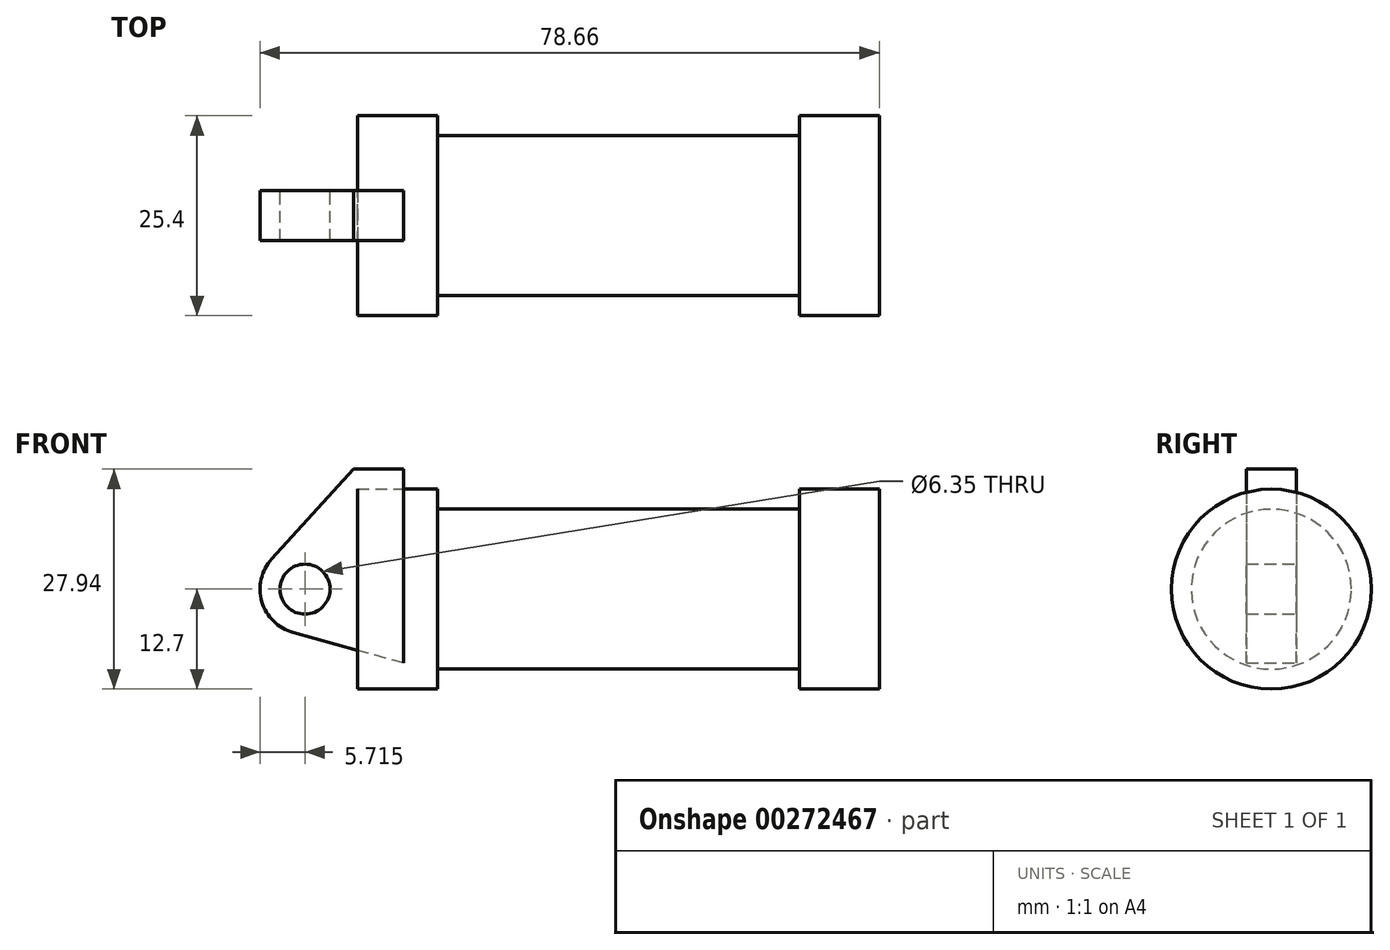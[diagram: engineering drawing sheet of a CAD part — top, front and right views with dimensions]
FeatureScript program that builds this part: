
annotation { "Feature Type Name" : "Feature", "Feature Type Description" : "" }
export const myFeature = defineFeature(function(context is Context, id is Id, definition is map)
    precondition{}
    {
        {
            var Q0;
            Q0=qCreatedBy(makeId("Front.planeOp"),FACE);
            var sketch = newSketch(context, id + "F0", { "sketchPlane" : qUnion([Q0])});
            skLineSegment(sketch, "E0", {"start": v(0, 0) * mm, "end": v(0, 12.7) * mm});
            skLineSegment(sketch, "E1", {"start": v(0, 12.7) * mm, "end": v(10.16, 12.7) * mm});
            skLineSegment(sketch, "E2", {"start": v(10.16, 12.7) * mm, "end": v(10.16, 10.16) * mm});
            skLineSegment(sketch, "E3", {"start": v(10.16, 10.16) * mm, "end": v(56.13, 10.16) * mm});
            skLineSegment(sketch, "E4", {"start": v(56.13, 10.16) * mm, "end": v(56.13, 12.7) * mm});
            skLineSegment(sketch, "E5", {"start": v(56.13, 12.7) * mm, "end": v(66.3, 12.7) * mm});
            skLineSegment(sketch, "E6", {"start": v(66.3, 12.7) * mm, "end": v(66.3, 0) * mm});
            skLineSegment(sketch, "E7", {"start": v(66.3, 0) * mm, "end": v(0, 0) * mm});
            skLineSegment(sketch, "E8", {"start": v(5.84, 15.24) * mm, "end": v(-0.5, 15.24) * mm});
            skLineSegment(sketch, "E9", {"start": v(-0.5, 15.24) * mm, "end": v(-10.88, 3.85) * mm});
            skLineSegment(sketch, "E10", {"start": v(0, 0) * mm, "end": v(-6.65, 0) * mm});
            skCircle(sketch, "E11", {"center": v(-6.65, 0) * mm, "radius": 5.72 * mm});
            skCircle(sketch, "E12", {"center": v(-6.65, 0) * mm, "radius": 3.18 * mm});
            skLineSegment(sketch, "E13", {"start": v(5.84, 15.24) * mm, "end": v(5.84, -9.4) * mm});
            skLineSegment(sketch, "E14", {"start": v(5.84, -9.4) * mm, "end": v(-8.18, -5.5) * mm});
            skSolve(sketch);
        }
        {
            var Q0;
            {var subQ0=sQuery(id+"F0.wireOp",EDGE,"E2");Q0=makeQuery(id+"F0.imprint","IMPRINT",FACE,{"disambiguationData":[TD([[makeQuery(id+"F0.imprint","IMPRINT",EDGE,{"derivedFrom":subQ0}),-1.0]])]});}
            var Q1;
            {var subQ0=sQuery(id+"F0.wireOp",EDGE,"E0");Q1=makeQuery(id+"F0.imprint","IMPRINT",FACE,{"disambiguationData":[TD([[makeQuery(id+"F0.imprint","IMPRINT",EDGE,{"derivedFrom":subQ0}),-1.0]])]});}
            var Q2;
            Q2=sQuery(id+"F0.wireOp",EDGE,"E7");
            revolve(context, id + "F1", {"entities" : qUnion([Q0, Q1]), "axis" : qUnion([Q2]), "revolveType" : RevolveType.FULL});
        }
        {
            var Q0;
            {var subQ3=sQuery(id+"F0.wireOp",EDGE,"E0");Q0=makeQuery(id+"F0.imprint","IMPRINT",FACE,{"disambiguationData":[TD([[makeQuery(id+"F0.imprint","IMPRINT",EDGE,{"derivedFrom":subQ3}),1.0]])]});}
            var Q1;
            {var subQ0=sQuery(id+"F0.wireOp",EDGE,"E0");Q1=makeQuery(id+"F0.imprint","IMPRINT",FACE,{"disambiguationData":[TD([[makeQuery(id+"F0.imprint","IMPRINT",EDGE,{"derivedFrom":subQ0}),-1.0]])]});}
            var Q2;
            {var subQ0=sQuery(id+"F0.wireOp",EDGE,"E14");Q2=makeQuery(id+"F0.imprint","IMPRINT",FACE,{"disambiguationData":[TD([[makeQuery(id+"F0.imprint","IMPRINT",EDGE,{"derivedFrom":subQ0}),-1.0]])]});}
            var Q3;
            {var subQ4=sQuery(id+"F0.wireOp",EDGE,"E12");Q3=makeQuery(id+"F0.imprint","IMPRINT",FACE,{"disambiguationData":[TD([[makeQuery(id+"F0.imprint","IMPRINT",EDGE,{"derivedFrom":subQ4}),-1.0]])]});}
            extrude(context, id + "F2", {"entities" : qUnion([Q0, Q1, Q2, Q3]), "endBound" : BoundingType.SYMMETRIC, "depth" : 6.35 * mm});
        }
    });
